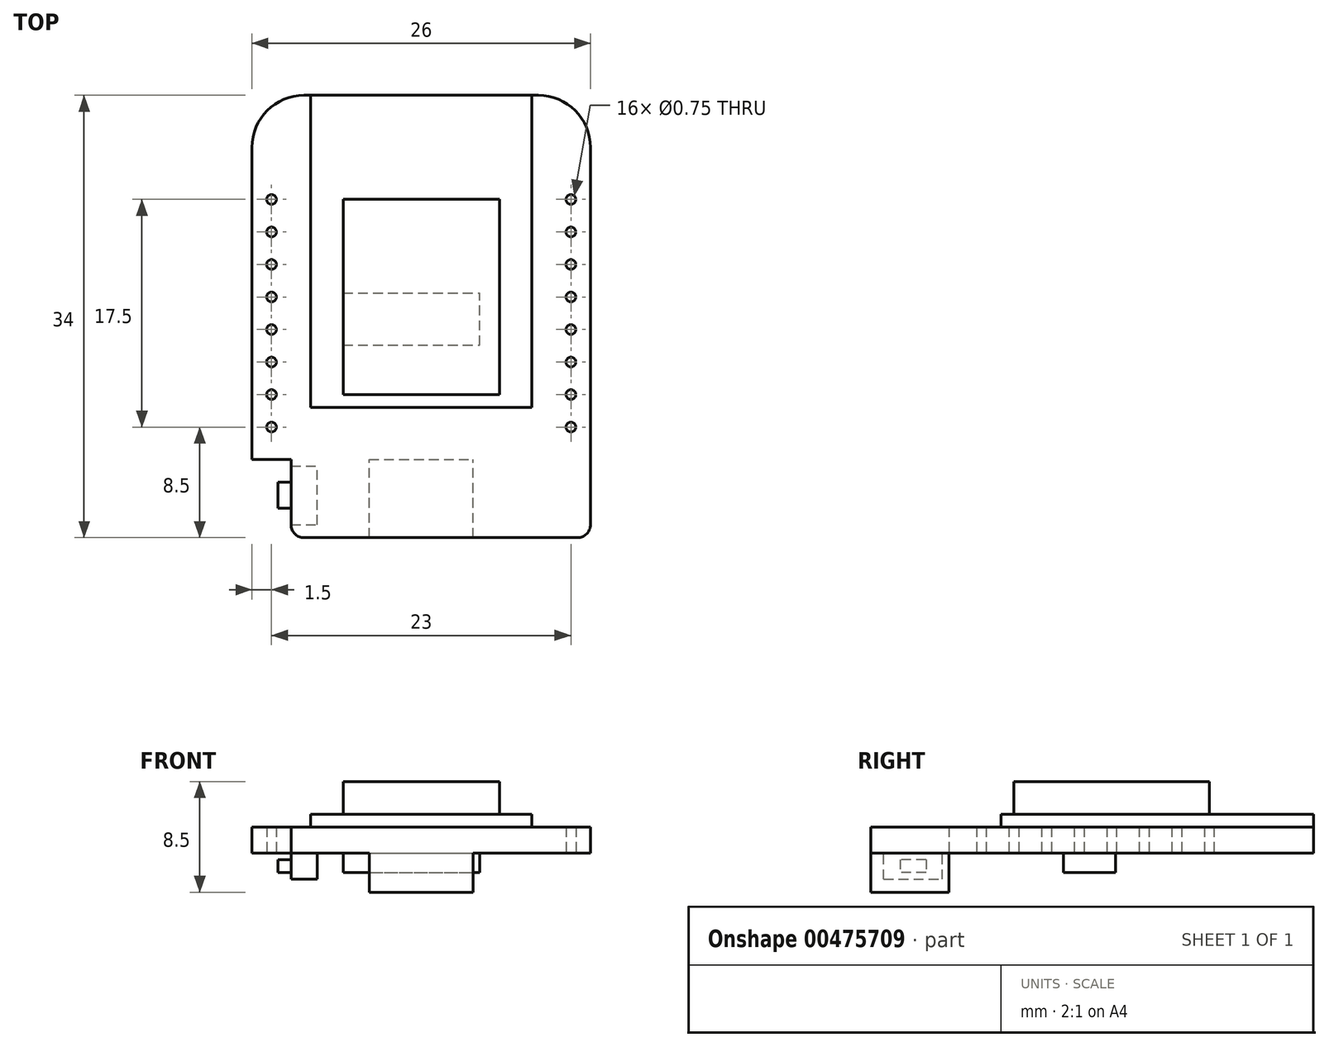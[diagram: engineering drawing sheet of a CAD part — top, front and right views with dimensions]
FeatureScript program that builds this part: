
annotation { "Feature Type Name" : "Feature", "Feature Type Description" : "" }
export const myFeature = defineFeature(function(context is Context, id is Id, definition is map)
    precondition{}
    {
        {
            var Q0;
            Q0=qCreatedBy(makeId("Top.planeOp"),FACE);
            var sketch = newSketch(context, id + "F0", { "sketchPlane" : qUnion([Q0])});
            skLineSegment(sketch, "E0.bottom", {"start": v(-13, 17) * mm, "end": v(13, 17) * mm});
            skLineSegment(sketch, "E0.top", {"start": v(-10, -17) * mm, "end": v(13, -17) * mm});
            skLineSegment(sketch, "E0.left", {"start": v(-13, 17) * mm, "end": v(-13, -11) * mm});
            skLineSegment(sketch, "E0.right", {"start": v(13, 17) * mm, "end": v(13, -17) * mm});
            skLineSegment(sketch, "E1.top", {"start": v(-13, -11) * mm, "end": v(-10, -11) * mm});
            skLineSegment(sketch, "E1.right", {"start": v(-10, -17) * mm, "end": v(-10, -11) * mm});
            skSolve(sketch);
        }
        {
            var Q0;
            Q0=qSketchRegion(id+"F0",true);
            extrude(context, id + "F1", {"entities" : qUnion([Q0]), "depth" : 2 * mm});
        }
        {
            var Q0;
            Q0=makeQuery(id+"F1.opExtrude","CAP_FACE",FACE,{"disambiguationData":[OSD([sQuery(id+"F0.wireOp",EDGE,"E0.bottom"),sQuery(id+"F0.wireOp",EDGE,"E0.top"),sQuery(id+"F0.wireOp",EDGE,"E0.left"),sQuery(id+"F0.wireOp",EDGE,"E0.right"),sQuery(id+"F0.wireOp",EDGE,"E1.bottom"),sQuery(id+"F0.wireOp",EDGE,"E1.left")])],"isStart":false});
            var sketch = newSketch(context, id + "F2", { "sketchPlane" : qUnion([Q0])});
            skLineSegment(sketch, "E2.bottom", {"start": v(-8.5, 17) * mm, "end": v(8.5, 17) * mm});
            skLineSegment(sketch, "E2.top", {"start": v(-8.5, -7) * mm, "end": v(8.5, -7) * mm});
            skLineSegment(sketch, "E2.left", {"start": v(-8.5, 17) * mm, "end": v(-8.5, -7) * mm});
            skLineSegment(sketch, "E2.right", {"start": v(8.5, 17) * mm, "end": v(8.5, -7) * mm});
            skSolve(sketch);
        }
        {
            var Q0;
            Q0=qSketchRegion(id+"F2",true);
            extrude(context, id + "F3", {"entities" : qUnion([Q0]), "operationType" : NewBodyOperationType.ADD, "depth" : 1 * mm});
        }
        {
            var Q0;
            Q0=makeQuery(id+"F3.opExtrude","CAP_FACE",FACE,{"disambiguationData":[OSD([sQuery(id+"F2.wireOp",EDGE,"E2.bottom"),sQuery(id+"F2.wireOp",EDGE,"E2.top"),sQuery(id+"F2.wireOp",EDGE,"E2.left"),sQuery(id+"F2.wireOp",EDGE,"E2.right")])],"isStart":false});
            var sketch = newSketch(context, id + "F4", { "sketchPlane" : qUnion([Q0])});
            skLineSegment(sketch, "E3.bottom", {"start": v(-6, 9) * mm, "end": v(6, 9) * mm});
            skLineSegment(sketch, "E3.top", {"start": v(-6, -6) * mm, "end": v(6, -6) * mm});
            skLineSegment(sketch, "E3.left", {"start": v(-6, 9) * mm, "end": v(-6, -6) * mm});
            skLineSegment(sketch, "E3.right", {"start": v(6, 9) * mm, "end": v(6, -6) * mm});
            skSolve(sketch);
        }
        {
            var Q0;
            Q0=qSketchRegion(id+"F4",true);
            extrude(context, id + "F5", {"entities" : qUnion([Q0]), "operationType" : NewBodyOperationType.ADD, "depth" : 2.5 * mm});
        }
        {
            var Q0;
            Q0=makeQuery(id+"F1.opExtrude","CAP_FACE",FACE,{"disambiguationData":[OSD([sQuery(id+"F0.wireOp",EDGE,"E0.bottom"),sQuery(id+"F0.wireOp",EDGE,"E0.top"),sQuery(id+"F0.wireOp",EDGE,"E0.left"),sQuery(id+"F0.wireOp",EDGE,"E0.right"),sQuery(id+"F0.wireOp",EDGE,"E1.top"),sQuery(id+"F0.wireOp",EDGE,"E1.right")])],"isStart":true});
            var sketch = newSketch(context, id + "F6", { "sketchPlane" : qUnion([Q0])});
            skLineSegment(sketch, "E4.bottom", {"start": v(-4, 17) * mm, "end": v(4, 17) * mm});
            skLineSegment(sketch, "E4.top", {"start": v(-4, 11) * mm, "end": v(4, 11) * mm});
            skLineSegment(sketch, "E4.left", {"start": v(-4, 17) * mm, "end": v(-4, 11) * mm});
            skLineSegment(sketch, "E4.right", {"start": v(4, 17) * mm, "end": v(4, 11) * mm});
            skSolve(sketch);
        }
        {
            var Q0;
            Q0=qSketchRegion(id+"F6",true);
            extrude(context, id + "F7", {"entities" : qUnion([Q0]), "operationType" : NewBodyOperationType.ADD, "depth" : 3 * mm});
        }
        {
            var Q0;
            Q0=makeQuery(id+"F1.opExtrude","CAP_FACE",FACE,{"disambiguationData":[OSD([sQuery(id+"F0.wireOp",EDGE,"E0.bottom"),sQuery(id+"F0.wireOp",EDGE,"E0.top"),sQuery(id+"F0.wireOp",EDGE,"E0.left"),sQuery(id+"F0.wireOp",EDGE,"E0.right"),sQuery(id+"F0.wireOp",EDGE,"E1.top"),sQuery(id+"F0.wireOp",EDGE,"E1.right")])],"isStart":true});
            var sketch = newSketch(context, id + "F8", { "sketchPlane" : qUnion([Q0])});
            skLineSegment(sketch, "E5.bottom", {"start": v(-10, 16) * mm, "end": v(-8, 16) * mm});
            skLineSegment(sketch, "E5.top", {"start": v(-10, 11.5) * mm, "end": v(-8, 11.5) * mm});
            skLineSegment(sketch, "E5.left", {"start": v(-10, 16) * mm, "end": v(-10, 11.5) * mm});
            skLineSegment(sketch, "E5.right", {"start": v(-8, 16) * mm, "end": v(-8, 11.5) * mm});
            skSolve(sketch);
        }
        {
            var Q0;
            Q0=qSketchRegion(id+"F8",true);
            extrude(context, id + "F9", {"entities" : qUnion([Q0]), "operationType" : NewBodyOperationType.ADD, "depth" : 2 * mm});
        }
        {
            var Q0;
            Q0=makeQuery(id+"F9.boolean.opBoolean","MERGE",FACE,{"derivedFrom":[makeQuery(id+"F1.opExtrude","SWEPT_FACE",FACE,{"disambiguationData":[OSD([sQuery(id+"F0.wireOp",EDGE,"E1.right")])]}),makeQuery(id+"F9.opExtrude","SWEPT_FACE",FACE,{"disambiguationData":[OSD([sQuery(id+"F8.wireOp",EDGE,"E5.left")])]})]});
            var sketch = newSketch(context, id + "F10", { "sketchPlane" : qUnion([Q0])});
            skLineSegment(sketch, "E6.bottom", {"start": v(12.75, -0.5) * mm, "end": v(14.75, -0.5) * mm});
            skLineSegment(sketch, "E6.top", {"start": v(12.75, -1.5) * mm, "end": v(14.75, -1.5) * mm});
            skLineSegment(sketch, "E6.left", {"start": v(12.75, -0.5) * mm, "end": v(12.75, -1.5) * mm});
            skLineSegment(sketch, "E6.right", {"start": v(14.75, -0.5) * mm, "end": v(14.75, -1.5) * mm});
            skSolve(sketch);
        }
        {
            var Q0;
            Q0=qSketchRegion(id+"F10",true);
            extrude(context, id + "F11", {"entities" : qUnion([Q0]), "operationType" : NewBodyOperationType.ADD, "depth" : 1 * mm});
        }
        {
            var Q0;
            Q0=makeQuery(id+"F1.opExtrude","CAP_FACE",FACE,{"disambiguationData":[OSD([sQuery(id+"F0.wireOp",EDGE,"E0.bottom"),sQuery(id+"F0.wireOp",EDGE,"E0.top"),sQuery(id+"F0.wireOp",EDGE,"E0.left"),sQuery(id+"F0.wireOp",EDGE,"E0.right"),sQuery(id+"F0.wireOp",EDGE,"E1.top"),sQuery(id+"F0.wireOp",EDGE,"E1.right")])],"isStart":true});
            var sketch = newSketch(context, id + "F12", { "sketchPlane" : qUnion([Q0])});
            skLineSegment(sketch, "E7.bottom", {"start": v(-6, 2.2) * mm, "end": v(4.5, 2.2) * mm});
            skLineSegment(sketch, "E7.top", {"start": v(-6, -1.8) * mm, "end": v(4.5, -1.8) * mm});
            skLineSegment(sketch, "E7.left", {"start": v(-6, 2.2) * mm, "end": v(-6, -1.8) * mm});
            skLineSegment(sketch, "E7.right", {"start": v(4.5, 2.2) * mm, "end": v(4.5, -1.8) * mm});
            skSolve(sketch);
        }
        {
            var Q0;
            Q0=qSketchRegion(id+"F12",true);
            extrude(context, id + "F13", {"entities" : qUnion([Q0]), "operationType" : NewBodyOperationType.ADD, "depth" : 1.5 * mm});
        }
        {
            var Q0;
            Q0=makeQuery(id+"F1.opExtrude","CAP_FACE",FACE,{"disambiguationData":[OSD([sQuery(id+"F0.wireOp",EDGE,"E0.bottom"),sQuery(id+"F0.wireOp",EDGE,"E0.top"),sQuery(id+"F0.wireOp",EDGE,"E0.left"),sQuery(id+"F0.wireOp",EDGE,"E0.right"),sQuery(id+"F0.wireOp",EDGE,"E1.top"),sQuery(id+"F0.wireOp",EDGE,"E1.right")])],"isStart":true});
            var sketch = newSketch(context, id + "F14", { "sketchPlane" : qUnion([Q0])});
            skCircle(sketch, "E8", {"center": v(-11.5, -9) * mm, "radius": 0.38 * mm});
            skCircle(sketch, "E9.0.1.0", {"center": v(-11.5, -6.5) * mm, "radius": 0.38 * mm});
            skCircle(sketch, "E9.0.2.0", {"center": v(-11.5, -4) * mm, "radius": 0.38 * mm});
            skCircle(sketch, "E9.0.3.0", {"center": v(-11.5, -1.5) * mm, "radius": 0.38 * mm});
            skCircle(sketch, "E9.0.4.0", {"center": v(-11.5, 1) * mm, "radius": 0.38 * mm});
            skCircle(sketch, "E9.0.5.0", {"center": v(-11.5, 3.5) * mm, "radius": 0.38 * mm});
            skCircle(sketch, "E9.0.6.0", {"center": v(-11.5, 6) * mm, "radius": 0.38 * mm});
            skCircle(sketch, "E9.0.7.0", {"center": v(-11.5, 8.5) * mm, "radius": 0.38 * mm});
            skLineSegment(sketch, "E9.direction1", {"start": v(-11.5, -9) * mm, "end": v(11.5, -9) * mm, "construction": true});
            skLineSegment(sketch, "E9.direction2", {"start": v(-11.5, -9) * mm, "end": v(-11.5, -6.5) * mm, "construction": true});
            skCircle(sketch, "E10.0.1.0", {"center": v(11.5, -9) * mm, "radius": 0.38 * mm});
            skCircle(sketch, "E10.0.1.1", {"center": v(11.5, -6.5) * mm, "radius": 0.38 * mm});
            skCircle(sketch, "E10.0.1.2", {"center": v(11.5, -4) * mm, "radius": 0.38 * mm});
            skCircle(sketch, "E10.0.1.3", {"center": v(11.5, -1.5) * mm, "radius": 0.38 * mm});
            skCircle(sketch, "E10.0.1.4", {"center": v(11.5, 1) * mm, "radius": 0.38 * mm});
            skCircle(sketch, "E10.0.1.5", {"center": v(11.5, 3.5) * mm, "radius": 0.38 * mm});
            skCircle(sketch, "E10.0.1.6", {"center": v(11.5, 6) * mm, "radius": 0.38 * mm});
            skCircle(sketch, "E10.0.1.7", {"center": v(11.5, 8.5) * mm, "radius": 0.38 * mm});
            skSolve(sketch);
        }
        {
            var Q0;
            Q0=qSketchRegion(id+"F14",true);
            extrude(context, id + "F15", {"entities" : qUnion([Q0]), "operationType" : NewBodyOperationType.REMOVE, "oppositeDirection" : true, "depth" : 25 * mm});
        }
        {
            var Q0;
            Q0=makeQuery(id+"F1.opExtrude","SWEPT_EDGE",EDGE,{"disambiguationData":[OSD([sQuery(id+"F0.wireOp",EDGE,"E0.bottom"),sQuery(id+"F0.wireOp",EDGE,"E0.left")])]});
            var Q1;
            Q1=makeQuery(id+"F1.opExtrude","SWEPT_EDGE",EDGE,{"disambiguationData":[OSD([sQuery(id+"F0.wireOp",EDGE,"E0.bottom"),sQuery(id+"F0.wireOp",EDGE,"E0.right")])]});
            fillet(context, id + "F16", {"entities" : qUnion([Q0, Q1]), "radius" : 4 * mm, "tangentPropagation" : true, "allowEdgeOverflow" : false});
        }
        {
            var Q0;
            Q0=makeQuery(id+"F1.opExtrude","SWEPT_EDGE",EDGE,{"disambiguationData":[OSD([sQuery(id+"F0.wireOp",EDGE,"E0.top"),sQuery(id+"F0.wireOp",EDGE,"E1.right")])]});
            var Q1;
            Q1=makeQuery(id+"F1.opExtrude","SWEPT_EDGE",EDGE,{"disambiguationData":[OSD([sQuery(id+"F0.wireOp",EDGE,"E0.top"),sQuery(id+"F0.wireOp",EDGE,"E0.right")])]});
            fillet(context, id + "F17", {"entities" : qUnion([Q0, Q1]), "radius" : 1 * mm, "tangentPropagation" : true, "allowEdgeOverflow" : false});
        }
    });
